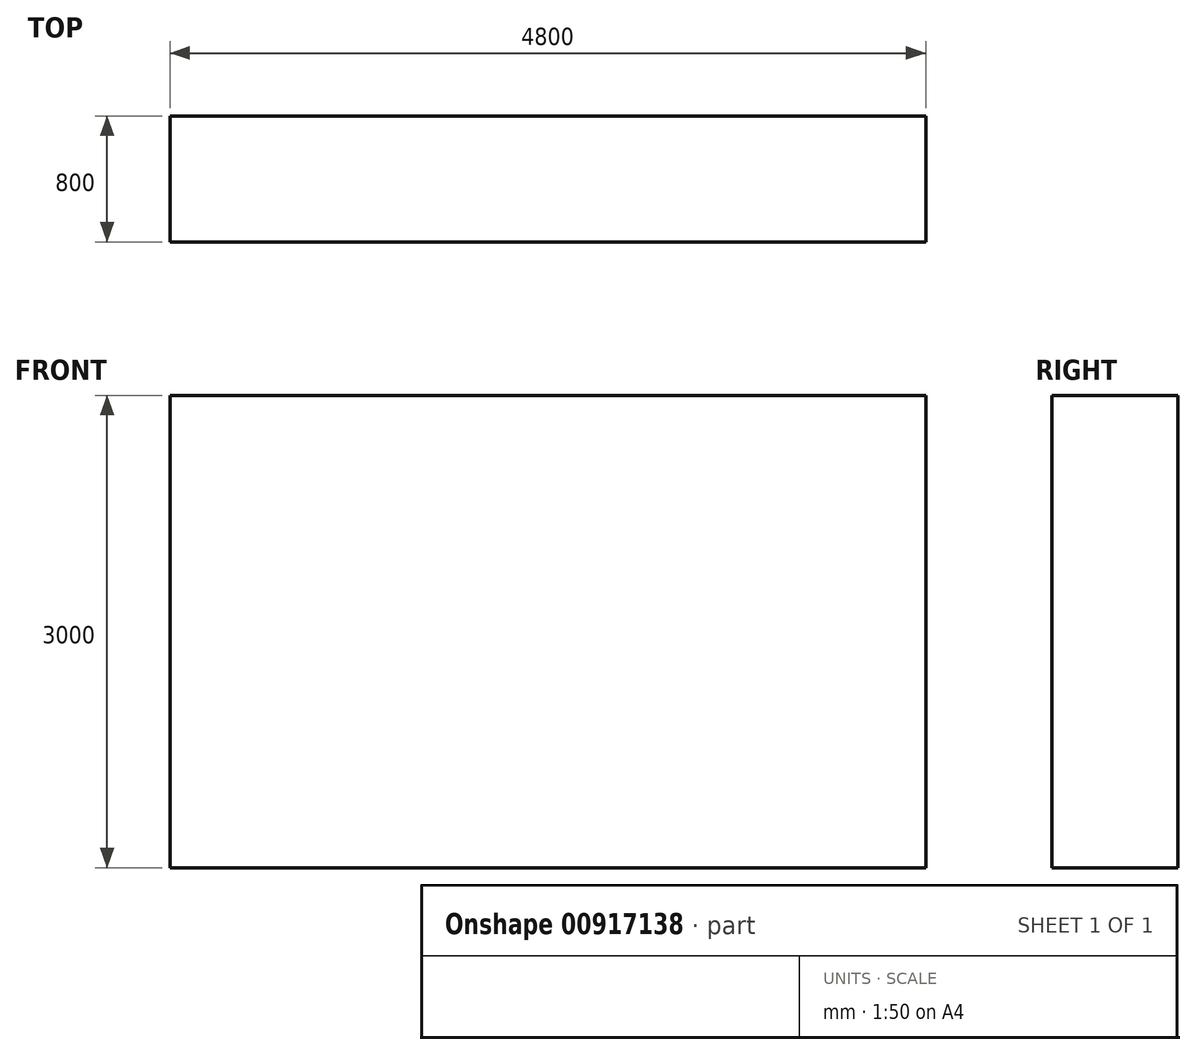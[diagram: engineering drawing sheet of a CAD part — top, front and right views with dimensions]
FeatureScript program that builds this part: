
annotation { "Feature Type Name" : "Feature", "Feature Type Description" : "" }
export const myFeature = defineFeature(function(context is Context, id is Id, definition is map)
    precondition{}
    {
        {
            var Q0;
            Q0=qCreatedBy(makeId("Top.planeOp"),FACE);
            var sketch = newSketch(context, id + "F0", { "sketchPlane" : qUnion([Q0])});
            skLineSegment(sketch, "E0.bottom", {"start": v(0, 0) * mm, "end": v(4800, 0) * mm});
            skLineSegment(sketch, "E0.top", {"start": v(0, 800) * mm, "end": v(4800, 800) * mm});
            skLineSegment(sketch, "E0.left", {"start": v(0, 0) * mm, "end": v(0, 800) * mm});
            skLineSegment(sketch, "E0.right", {"start": v(4800, 0) * mm, "end": v(4800, 800) * mm});
            skSolve(sketch);
        }
        {
            var Q0;
            Q0=makeQuery(id+"F0.imprint","IMPRINT",FACE,{"disambiguationData":[TD([[makeQuery(id+"F0.imprint","IMPRINT",EDGE,{"derivedFrom":sQuery(id+"F0.wireOp",EDGE,"E0.bottom")}),1.0]])]});
            extrude(context, id + "F1", {"entities" : qUnion([Q0]), "depth" : 3000 * mm, "offsetDistance" : 25 * mm});
        }
    });
